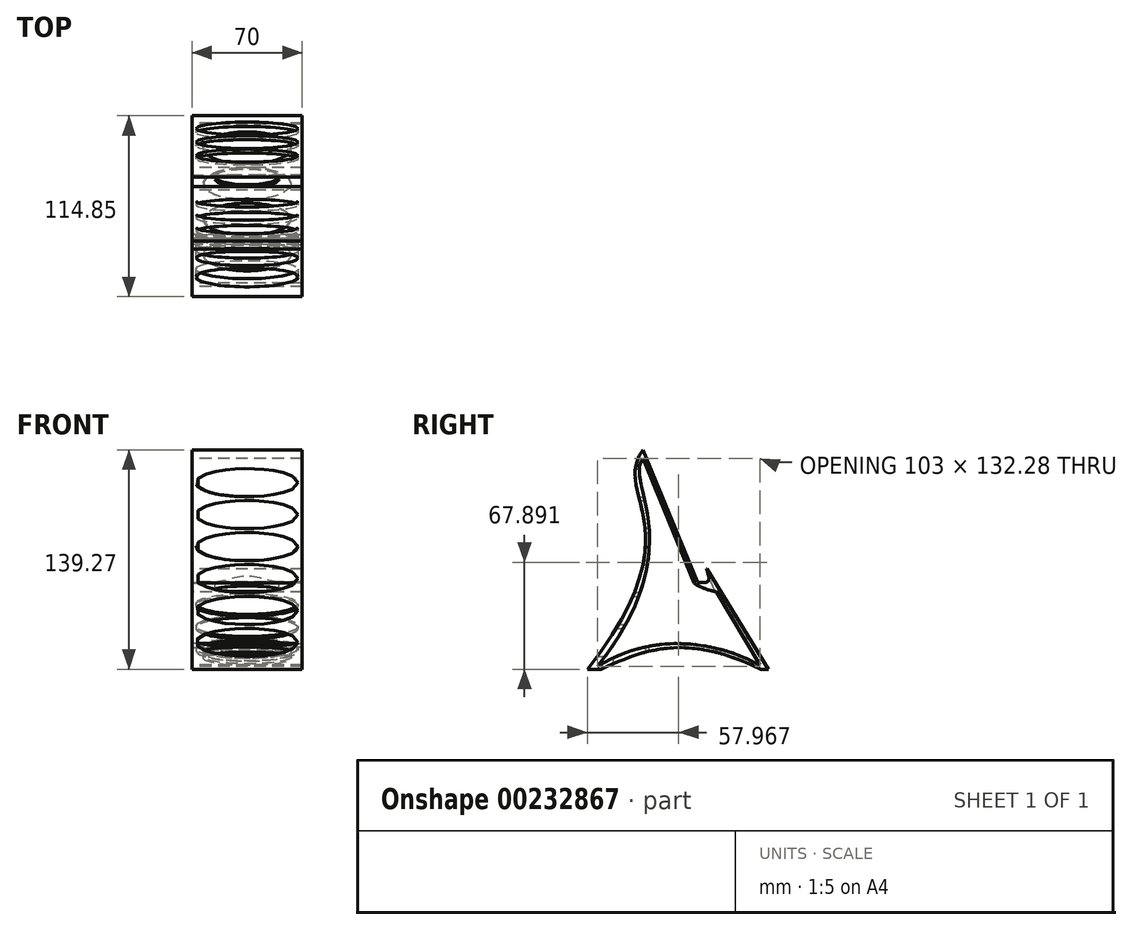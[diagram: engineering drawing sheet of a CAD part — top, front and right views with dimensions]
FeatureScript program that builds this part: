
annotation { "Feature Type Name" : "Feature", "Feature Type Description" : "" }
export const myFeature = defineFeature(function(context is Context, id is Id, definition is map)
    precondition{}
    {
        {
            var Q0;
            Q0=qCreatedBy(makeId("Right.planeOp"),FACE);
            var sketch = newSketch(context, id + "F0", { "sketchPlane" : qUnion([Q0])});
            skFitSpline(sketch, "E0", {"points": [v(-65.05, 0) * mm, v(-29.92, 139.27) * mm], "startDerivative": vector(210.97, 269.62) * mm, "endDerivative": vector(62.07, 87.75) * mm});
            skFitSpline(sketch, "E1", {"points": [v(-56.41, 0) * mm, v(45.2, 0) * mm], "startDerivative": vector(85.43, 39.38) * mm, "endDerivative": vector(140.76, -68.45) * mm});
            skFitSpline(sketch, "E2", {"points": [v(49.8, 0) * mm, v(10.74, 63.83) * mm], "startDerivative": vector(-39.06, 63.83) * mm, "endDerivative": vector(-39.06, 63.83) * mm});
            skLineSegment(sketch, "E3", {"start": v(-29.92, 139.27) * mm, "end": v(4.83, 55.39) * mm});
            skFitSpline(sketch, "E4", {"points": [v(-58.58, 1.75) * mm, v(-29.9, 134.03) * mm], "startDerivative": vector(181.66, 231.88) * mm, "endDerivative": vector(35.66, 50.36) * mm});
            skFitSpline(sketch, "E5", {"points": [v(-58.58, 1.75) * mm, v(44.42, 2.6) * mm], "startDerivative": vector(96.07, 60.59) * mm, "endDerivative": vector(95.42, -52.13) * mm});
            skFitSpline(sketch, "E6", {"points": [v(4.83, 55.39) * mm, v(10.74, 63.83) * mm], "startDerivative": vector(36.77, -7.47) * mm, "endDerivative": vector(2.44, 4) * mm});
            skLineSegment(sketch, "E7", {"start": v(-65.05, 0) * mm, "end": v(-56.41, 0) * mm});
            skLineSegment(sketch, "E8", {"start": v(45.2, 0) * mm, "end": v(49.8, 0) * mm});
            skLineSegment(sketch, "E9", {"start": v(16.98, 49.19) * mm, "end": v(44.42, 2.6) * mm});
            skLineSegment(sketch, "E10", {"start": v(-29.9, 134.03) * mm, "end": v(2.49, 54.83) * mm});
            skFitSpline(sketch, "E11", {"points": [v(2.49, 54.83) * mm, v(16.98, 49.19) * mm], "startDerivative": vector(13.4, -9.27) * mm, "endDerivative": vector(11.5, -1.96) * mm});
            skSolve(sketch);
        }
        {
            var Q0;
            Q0=makeQuery(id+"F0.imprint","IMPRINT",FACE,{"disambiguationData":[TD([[makeQuery(id+"F0.imprint","IMPRINT",EDGE,{"derivedFrom":sQuery(id+"F0.wireOp",EDGE,"E0")}),-1.0]])]});
            extrude(context, id + "F1", {"entities" : qUnion([Q0]), "depth" : 70 * mm});
        }
        {
            var Q0;
            Q0=makeQuery(id+"F1.opExtrude","SWEPT_FACE",FACE,{"disambiguationData":[OSD([sQuery(id+"F0.wireOp",EDGE,"E9")])]});
            var sketch = newSketch(context, id + "F2", { "sketchPlane" : qUnion([Q0])});
            skEllipse(sketch, "E12", {"center": v(35, 23.43) * mm, "majorRadius": 32.5 * mm, "minorRadius": 7.82 * mm, "majorAxis": v(1, 0)});
            skEllipse(sketch, "E13.0.1.0", {"center": v(35, 6.93) * mm, "majorRadius": 32.5 * mm, "minorRadius": 7.82 * mm, "majorAxis": v(1, 0)});
            skEllipse(sketch, "E13.0.2.0", {"center": v(35, -9.57) * mm, "majorRadius": 32.5 * mm, "minorRadius": 7.82 * mm, "majorAxis": v(1, 0)});
            skLineSegment(sketch, "E13.direction1", {"start": v(35, 23.43) * mm, "end": v(57.03, 23.43) * mm, "construction": true});
            skLineSegment(sketch, "E13.direction2", {"start": v(35, 23.43) * mm, "end": v(35, 6.93) * mm, "construction": true});
            skSolve(sketch);
        }
        {
            var Q0;
            Q0=qSketchRegion(id+"F2",true);
            var Q1;
            Q1=makeQuery(id+"F1.opExtrude","SWEPT_FACE",FACE,{"disambiguationData":[OSD([sQuery(id+"F0.wireOp",EDGE,"E2")])]});
            extrude(context, id + "F3", {"entities" : qUnion([Q0]), "operationType" : NewBodyOperationType.REMOVE, "endBound" : BoundingType.UP_TO_SURFACE, "oppositeDirection" : true, "endBoundEntityFace" : qUnion([Q1]), "depth" : 25 * mm});
        }
        {
            var Q0;
            Q0=qCreatedBy(makeId("Top.planeOp"),FACE);
            var sketch = newSketch(context, id + "F4", { "sketchPlane" : qUnion([Q0])});
            skEllipse(sketch, "E14", {"center": v(35, -38.54) * mm, "majorRadius": 27.85 * mm, "minorRadius": 10.2 * mm, "majorAxis": v(1, 0)});
            skEllipse(sketch, "E15.0.1.0", {"center": v(35, -15.94) * mm, "majorRadius": 27.85 * mm, "minorRadius": 10.2 * mm, "majorAxis": v(1, 0)});
            skEllipse(sketch, "E15.0.2.0", {"center": v(35, 6.66) * mm, "majorRadius": 27.85 * mm, "minorRadius": 10.2 * mm, "majorAxis": v(1, 0)});
            skEllipse(sketch, "E15.0.3.0", {"center": v(35, 29.26) * mm, "majorRadius": 27.85 * mm, "minorRadius": 10.2 * mm, "majorAxis": v(1, 0)});
            skLineSegment(sketch, "E15.direction1", {"start": v(35, -38.54) * mm, "end": v(60, -38.54) * mm, "construction": true});
            skLineSegment(sketch, "E15.direction2", {"start": v(35, -38.54) * mm, "end": v(35, -15.94) * mm, "construction": true});
            skSolve(sketch);
        }
        {
            var Q0;
            Q0=qSketchRegion(id+"F4",true);
            var Q1;
            Q1=makeQuery(id+"F1.opExtrude","SWEPT_FACE",FACE,{"disambiguationData":[OSD([sQuery(id+"F0.wireOp",EDGE,"E5")])]});
            extrude(context, id + "F5", {"entities" : qUnion([Q0]), "operationType" : NewBodyOperationType.REMOVE, "endBound" : BoundingType.UP_TO_SURFACE, "endBoundEntityFace" : qUnion([Q1]), "depth" : 25 * mm});
        }
        {
            var Q0;
            Q0=qCreatedBy(makeId("Front.planeOp"),FACE);
            cPlane(context, id + "F6", {"entities" : qUnion([Q0]), "cplaneType" : CPlaneType.OFFSET, "offset" : 70 * mm, "width" : 150 * mm, "height" : 150 * mm});
        }
        {
            var Q0;
            Q0=qCreatedBy(id+"F6.planeOp",FACE);
            var sketch = newSketch(context, id + "F7", { "sketchPlane" : qUnion([Q0])});
            skEllipse(sketch, "E16", {"center": v(35, 118.52) * mm, "majorRadius": 32.5 * mm, "minorRadius": 8.93 * mm, "majorAxis": v(1, 0)});
            skEllipse(sketch, "E17.0.1.0", {"center": v(35, 98.22) * mm, "majorRadius": 32.5 * mm, "minorRadius": 8.93 * mm, "majorAxis": v(1, 0)});
            skEllipse(sketch, "E17.0.2.0", {"center": v(35, 77.92) * mm, "majorRadius": 32.5 * mm, "minorRadius": 8.93 * mm, "majorAxis": v(1, 0)});
            skEllipse(sketch, "E17.0.3.0", {"center": v(35, 57.62) * mm, "majorRadius": 32.5 * mm, "minorRadius": 8.93 * mm, "majorAxis": v(1, 0)});
            skEllipse(sketch, "E17.0.4.0", {"center": v(35, 37.32) * mm, "majorRadius": 32.5 * mm, "minorRadius": 8.93 * mm, "majorAxis": v(1, 0)});
            skEllipse(sketch, "E17.0.5.0", {"center": v(35, 17.02) * mm, "majorRadius": 32.5 * mm, "minorRadius": 8.93 * mm, "majorAxis": v(1, 0)});
            skLineSegment(sketch, "E17.direction1", {"start": v(35, 118.52) * mm, "end": v(60, 118.52) * mm, "construction": true});
            skLineSegment(sketch, "E17.direction2", {"start": v(35, 118.52) * mm, "end": v(35, 98.22) * mm, "construction": true});
            skSolve(sketch);
        }
        {
            var Q0;
            Q0=makeQuery(id+"F7.imprint","IMPRINT",FACE,{"disambiguationData":[TD([[makeQuery(id+"F7.imprint","IMPRINT",EDGE,{"derivedFrom":sQuery(id+"F7.wireOp",EDGE,"E17.0.3.0")}),1.0]])]});
            var Q1;
            Q1=makeQuery(id+"F7.imprint","IMPRINT",FACE,{"disambiguationData":[TD([[makeQuery(id+"F7.imprint","IMPRINT",EDGE,{"derivedFrom":sQuery(id+"F7.wireOp",EDGE,"E17.0.4.0")}),1.0]])]});
            var Q2;
            Q2=makeQuery(id+"F7.imprint","IMPRINT",FACE,{"disambiguationData":[TD([[makeQuery(id+"F7.imprint","IMPRINT",EDGE,{"derivedFrom":sQuery(id+"F7.wireOp",EDGE,"E17.0.5.0")}),1.0]])]});
            var Q3;
            Q3=makeQuery(id+"F1.opExtrude","SWEPT_FACE",FACE,{"disambiguationData":[OSD([sQuery(id+"F0.wireOp",EDGE,"E4")])]});
            extrude(context, id + "F8", {"entities" : qUnion([Q0, Q1, Q2]), "operationType" : NewBodyOperationType.REMOVE, "endBound" : BoundingType.UP_TO_SURFACE, "oppositeDirection" : true, "endBoundEntityFace" : qUnion([Q3]), "depth" : 25 * mm});
        }
        {
            var Q0;
            Q0=makeQuery(id+"F7.imprint","IMPRINT",FACE,{"disambiguationData":[TD([[makeQuery(id+"F7.imprint","IMPRINT",EDGE,{"derivedFrom":sQuery(id+"F7.wireOp",EDGE,"E16")}),1.0]])]});
            var Q1;
            Q1=makeQuery(id+"F7.imprint","IMPRINT",FACE,{"disambiguationData":[TD([[makeQuery(id+"F7.imprint","IMPRINT",EDGE,{"derivedFrom":sQuery(id+"F7.wireOp",EDGE,"E17.0.1.0")}),1.0]])]});
            var Q2;
            Q2=makeQuery(id+"F7.imprint","IMPRINT",FACE,{"disambiguationData":[TD([[makeQuery(id+"F7.imprint","IMPRINT",EDGE,{"derivedFrom":sQuery(id+"F7.wireOp",EDGE,"E17.0.2.0")}),1.0]])]});
            var Q3;
            Q3=makeQuery(id+"F1.opExtrude","SWEPT_FACE",FACE,{"disambiguationData":[OSD([sQuery(id+"F0.wireOp",EDGE,"E3")])]});
            extrude(context, id + "F9", {"entities" : qUnion([Q0, Q1, Q2]), "operationType" : NewBodyOperationType.REMOVE, "endBound" : BoundingType.UP_TO_SURFACE, "oppositeDirection" : true, "endBoundEntityFace" : qUnion([Q3]), "depth" : 25 * mm});
        }
        {
            var Q0;
            Q0=makeQuery(id+"F1.opExtrude","SWEPT_FACE",FACE,{"disambiguationData":[OSD([sQuery(id+"F0.wireOp",EDGE,"E3")])]});
            var Q1;
            Q1=makeQuery(id+"F1.opExtrude","SWEPT_EDGE",EDGE,{"disambiguationData":[OSD([sQuery(id+"F0.wireOp",EDGE,"E0"),sQuery(id+"F0.wireOp",EDGE,"E3")])]});
            cPlane(context, id + "F10", {"entities" : qUnion([Q0, Q1]), "cplaneType" : CPlaneType.LINE_ANGLE, "offset" : 25 * mm, "angle" : 90 * degree, "width" : 150 * mm, "height" : 150 * mm});
        }
        {
            var Q0;
            Q0=qCreatedBy(id+"F10.planeOp",FACE);
            var sketch = newSketch(context, id + "F11", { "sketchPlane" : qUnion([Q0])});
            skEllipse(sketch, "E18", {"center": v(35, 29.66) * mm, "majorRadius": 20.28 * mm, "minorRadius": 4 * mm, "majorAxis": v(-1, 0)});
            skSolve(sketch);
        }
        {
            var Q0;
            Q0 = qSketchRegion(id + "F11", true);
            var Q1;
            Q1=makeQuery(id+"F1.opExtrude","SWEPT_FACE",FACE,{"disambiguationData":[OSD([sQuery(id+"F0.wireOp",EDGE,"E11")])]});
            extrude(context, id + "F12", {"entities" : qUnion([Q0]), "operationType" : NewBodyOperationType.REMOVE, "endBound" : BoundingType.UP_TO_SURFACE, "oppositeDirection" : true, "endBoundEntityFace" : qUnion([Q1]), "depth" : 25 * mm});
        }
    });
